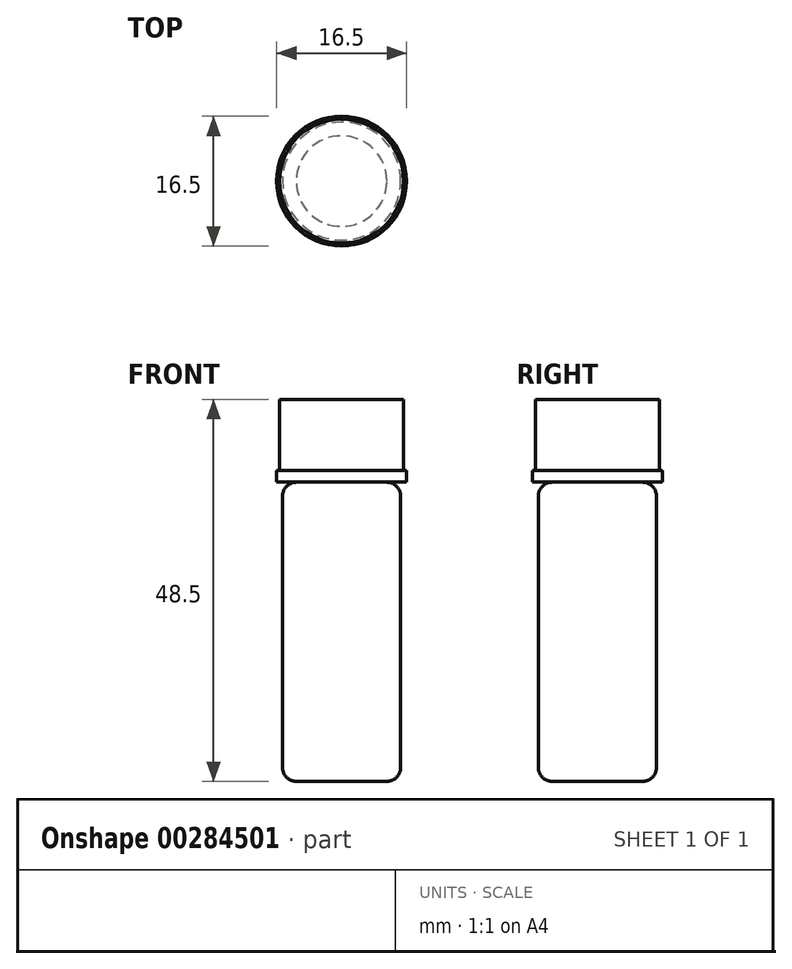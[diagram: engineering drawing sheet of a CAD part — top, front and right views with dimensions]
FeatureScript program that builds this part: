
annotation { "Feature Type Name" : "Feature", "Feature Type Description" : "" }
export const myFeature = defineFeature(function(context is Context, id is Id, definition is map)
    precondition{}
    {
        {
            var Q0;
            Q0=qCreatedBy(makeId("Top.planeOp"),FACE);
            var sketch = newSketch(context, id + "F0", { "sketchPlane" : qUnion([Q0])});
            skCircle(sketch, "E0", {"center": v(0, 0) * mm, "radius": 7.5 * mm});
            skSolve(sketch);
        }
        {
            var Q0;
            Q0 = qSketchRegion(id + "F0", true);
            extrude(context, id + "F1", {"entities" : qUnion([Q0]), "depth" : 38 * mm});
        }
        {
            var Q0;
            Q0=makeQuery(id+"F1.opExtrude","CAP_FACE",FACE,{"disambiguationData":[OSD([sQuery(id+"F0.wireOp",EDGE,"E0")])],"isStart":false});
            var sketch = newSketch(context, id + "F2", { "sketchPlane" : qUnion([Q0])});
            skCircle(sketch, "E1", {"center": v(0, 0) * mm, "radius": 5.75 * mm});
            skSolve(sketch);
        }
        {
            var Q0;
            Q0=makeQuery(id+"F1.opExtrude","CAP_EDGE",EDGE,{"disambiguationData":[OSD([sQuery(id+"F0.wireOp",EDGE,"E0")])],"isStart":false});
            var Q1;
            Q1=makeQuery(id+"F1.opExtrude","CAP_EDGE",EDGE,{"disambiguationData":[OSD([sQuery(id+"F0.wireOp",EDGE,"E0")])],"isStart":true});
            fillet(context, id + "F3", {"entities" : qUnion([Q0, Q1]), "radius" : 1.75 * mm, "tangentPropagation" : true, "allowEdgeOverflow" : false});
        }
        {
            var Q0;
            Q0=makeQuery(id+"F2.imprint","IMPRINT",FACE,{"disambiguationData":[TD([[makeQuery(id+"F2.imprint","IMPRINT",EDGE,{"derivedFrom":sQuery(id+"F2.wireOp",EDGE,"E1")}),1.0]])]});
            var sketch = newSketch(context, id + "F4", { "sketchPlane" : qUnion([Q0])});
            skCircle(sketch, "E2", {"center": v(0, 0) * mm, "radius": 8.25 * mm});
            skSolve(sketch);
        }
        {
            var Q0;
            Q0 = qSketchRegion(id + "F4", true);
            extrude(context, id + "F5", {"entities" : qUnion([Q0]), "operationType" : NewBodyOperationType.ADD, "depth" : 1.5 * mm});
        }
        {
            var Q0;
            Q0=makeQuery(id+"F5.opExtrude","CAP_FACE",FACE,{"disambiguationData":[OSD([sQuery(id+"F4.wireOp",EDGE,"E2")])],"isStart":false});
            var sketch = newSketch(context, id + "F6", { "sketchPlane" : qUnion([Q0])});
            skCircle(sketch, "E3", {"center": v(0, 0) * mm, "radius": 7.88 * mm});
            skSolve(sketch);
        }
        {
            var Q0;
            Q0 = qSketchRegion(id + "F6", true);
            extrude(context, id + "F7", {"entities" : qUnion([Q0]), "operationType" : NewBodyOperationType.ADD, "depth" : 9 * mm});
        }
    });
